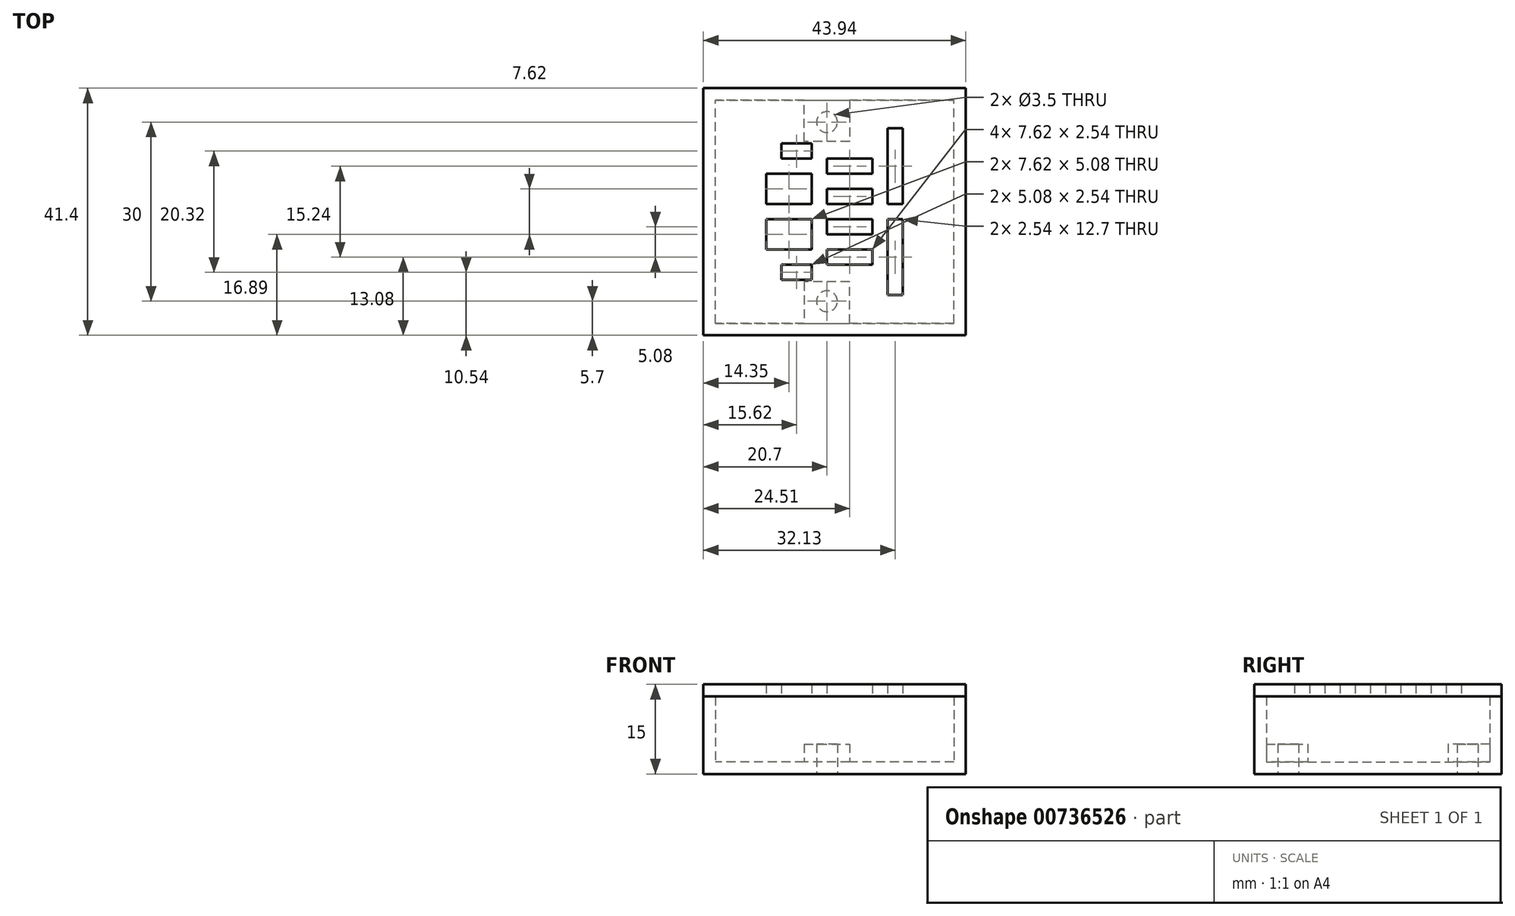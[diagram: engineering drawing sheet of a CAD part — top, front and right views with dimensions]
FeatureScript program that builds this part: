
annotation { "Feature Type Name" : "Feature", "Feature Type Description" : "" }
export const myFeature = defineFeature(function(context is Context, id is Id, definition is map)
    precondition{}
    {
        {
            var Q0;
            Q0=qCreatedBy(makeId("Top.planeOp"),FACE);
            var sketch = newSketch(context, id + "F0", { "sketchPlane" : qUnion([Q0])});
            skLineSegment(sketch, "E0.bottom", {"start": v(-13.97, 12.7) * mm, "end": v(13.97, 12.7) * mm, "construction": true});
            skLineSegment(sketch, "E0.top", {"start": v(-13.97, -12.7) * mm, "end": v(13.97, -12.7) * mm, "construction": true});
            skLineSegment(sketch, "E0.left", {"start": v(-13.97, 12.7) * mm, "end": v(-13.97, -12.7) * mm, "construction": true});
            skLineSegment(sketch, "E0.right", {"start": v(13.97, 12.7) * mm, "end": v(13.97, -12.7) * mm, "construction": true});
            skCircle(sketch, "E1", {"center": v(-13.97, 12.7) * mm, "radius": 1.25 * mm, "construction": true});
            skCircle(sketch, "E2", {"center": v(13.97, 12.7) * mm, "radius": 1.25 * mm, "construction": true});
            skCircle(sketch, "E3", {"center": v(13.97, -12.7) * mm, "radius": 1.25 * mm, "construction": true});
            skCircle(sketch, "E4", {"center": v(-13.97, -12.7) * mm, "radius": 1.25 * mm, "construction": true});
            skLineSegment(sketch, "E5.0", {"start": v(-19.97, 18.7) * mm, "end": v(-19.97, -18.7) * mm});
            skLineSegment(sketch, "E5.1", {"start": v(-19.97, 18.7) * mm, "end": v(19.97, 18.7) * mm});
            skLineSegment(sketch, "E5.2", {"start": v(19.97, 18.7) * mm, "end": v(19.97, -18.7) * mm});
            skLineSegment(sketch, "E5.3", {"start": v(-19.97, -18.7) * mm, "end": v(19.97, -18.7) * mm});
            skLineSegment(sketch, "E6.0", {"start": v(-21.97, 20.7) * mm, "end": v(-21.97, -20.7) * mm});
            skLineSegment(sketch, "E6.1", {"start": v(-21.97, 20.7) * mm, "end": v(21.97, 20.7) * mm});
            skLineSegment(sketch, "E6.2", {"start": v(21.97, 20.7) * mm, "end": v(21.97, -20.7) * mm});
            skLineSegment(sketch, "E6.3", {"start": v(-21.97, -20.7) * mm, "end": v(21.97, -20.7) * mm});
            skLineSegment(sketch, "E7", {"start": v(-1.27, -15) * mm, "end": v(-1.27, 15) * mm, "construction": true});
            skPoint(sketch, "E8", {"position": v(-1.27, 0) * mm});
            skCircle(sketch, "E9", {"center": v(-1.27, 15) * mm, "radius": 1.75 * mm});
            skCircle(sketch, "E10", {"center": v(-1.27, -15) * mm, "radius": 1.75 * mm});
            skLineSegment(sketch, "E11", {"start": v(-5.08, 18.7) * mm, "end": v(-5.08, 11.75) * mm});
            skLineSegment(sketch, "E12", {"start": v(-5.08, 11.75) * mm, "end": v(2.54, 11.75) * mm});
            skLineSegment(sketch, "E13", {"start": v(2.54, 11.75) * mm, "end": v(2.54, 18.7) * mm});
            skPoint(sketch, "E14", {"position": v(-1.27, 11.75) * mm});
            skLineSegment(sketch, "E15", {"start": v(-5.08, -18.7) * mm, "end": v(-5.08, -11.75) * mm});
            skLineSegment(sketch, "E16", {"start": v(-5.08, -11.75) * mm, "end": v(2.54, -11.75) * mm});
            skLineSegment(sketch, "E17", {"start": v(2.54, -11.75) * mm, "end": v(2.54, -18.7) * mm});
            skSolve(sketch);
        }
        {
            var Q0;
            Q0=qSketchRegion(id+"F0",true);
            var Q1;
            Q1=makeQuery(id+"F0.imprint","IMPRINT",FACE,{"disambiguationData":[TD([[makeQuery(id+"F0.imprint","IMPRINT",EDGE,{"derivedFrom":sQuery(id+"F0.wireOp",EDGE,"E5.0")}),1.0]])]});
            var Q2;
            Q2=makeQuery(id+"F0.imprint","IMPRINT",FACE,{"disambiguationData":[TD([[makeQuery(id+"F0.imprint","IMPRINT",EDGE,{"derivedFrom":sQuery(id+"F0.wireOp",EDGE,"E4")}),-1.0]])]});
            var Q3;
            Q3=makeQuery(id+"F0.imprint","IMPRINT",FACE,{"disambiguationData":[TD([[makeQuery(id+"F0.imprint","IMPRINT",EDGE,{"derivedFrom":sQuery(id+"F0.wireOp",EDGE,"E1")}),-1.0]])]});
            var Q4;
            Q4=makeQuery(id+"F0.imprint","IMPRINT",FACE,{"disambiguationData":[TD([[makeQuery(id+"F0.imprint","IMPRINT",EDGE,{"derivedFrom":sQuery(id+"F0.wireOp",EDGE,"E2")}),-1.0]])]});
            var Q5;
            Q5=makeQuery(id+"F0.imprint","IMPRINT",FACE,{"disambiguationData":[TD([[makeQuery(id+"F0.imprint","IMPRINT",EDGE,{"derivedFrom":sQuery(id+"F0.wireOp",EDGE,"E3")}),-1.0]])]});
            var Q6;
            Q6=makeQuery(id+"F0.imprint","IMPRINT",FACE,{"disambiguationData":[TD([[makeQuery(id+"F0.imprint","IMPRINT",EDGE,{"derivedFrom":sQuery(id+"F0.wireOp",EDGE,"E9")}),-1.0]])]});
            var Q7;
            Q7=makeQuery(id+"F0.imprint","IMPRINT",FACE,{"disambiguationData":[TD([[makeQuery(id+"F0.imprint","IMPRINT",EDGE,{"derivedFrom":sQuery(id+"F0.wireOp",EDGE,"E10")}),-1.0]])]});
            extrude(context, id + "F1", {"entities" : qUnion([Q0, Q1, Q2, Q3, Q4, Q5, Q6, Q7]), "depth" : 2 * mm, "offsetDistance" : 25 * mm});
        }
        {
            var Q0;
            Q0=makeQuery(id+"F0.imprint","IMPRINT",FACE,{"disambiguationData":[TD([[makeQuery(id+"F0.imprint","IMPRINT",EDGE,{"derivedFrom":sQuery(id+"F0.wireOp",EDGE,"E5.0")}),-1.0]])]});
            var Q1;
            Q1=makeQuery(id+"F0.imprint","IMPRINT",FACE,{"disambiguationData":[TD([[makeQuery(id+"F0.imprint","IMPRINT",EDGE,{"derivedFrom":sQuery(id+"F0.wireOp",EDGE,"E3")}),-1.0]])]});
            var Q2;
            Q2=makeQuery(id+"F0.imprint","IMPRINT",FACE,{"disambiguationData":[TD([[makeQuery(id+"F0.imprint","IMPRINT",EDGE,{"derivedFrom":sQuery(id+"F0.wireOp",EDGE,"E4")}),-1.0]])]});
            var Q3;
            Q3=makeQuery(id+"F0.imprint","IMPRINT",FACE,{"disambiguationData":[TD([[makeQuery(id+"F0.imprint","IMPRINT",EDGE,{"derivedFrom":sQuery(id+"F0.wireOp",EDGE,"E1")}),-1.0]])]});
            var Q4;
            Q4=makeQuery(id+"F0.imprint","IMPRINT",FACE,{"disambiguationData":[TD([[makeQuery(id+"F0.imprint","IMPRINT",EDGE,{"derivedFrom":sQuery(id+"F0.wireOp",EDGE,"E2")}),-1.0]])]});
            extrude(context, id + "F2", {"entities" : qUnion([Q0, Q1, Q2, Q3, Q4]), "operationType" : NewBodyOperationType.ADD, "depth" : 13 * mm, "offsetDistance" : 25 * mm});
        }
        {
            var Q0;
            Q0=makeQuery(id+"F0.imprint","IMPRINT",FACE,{"disambiguationData":[TD([[makeQuery(id+"F0.imprint","IMPRINT",EDGE,{"derivedFrom":sQuery(id+"F0.wireOp",EDGE,"E9")}),-1.0]])]});
            var Q1;
            Q1=makeQuery(id+"F0.imprint","IMPRINT",FACE,{"disambiguationData":[TD([[makeQuery(id+"F0.imprint","IMPRINT",EDGE,{"derivedFrom":sQuery(id+"F0.wireOp",EDGE,"E10")}),-1.0]])]});
            extrude(context, id + "F3", {"entities" : qUnion([Q0, Q1]), "operationType" : NewBodyOperationType.ADD, "depth" : 5 * mm, "offsetDistance" : 25 * mm});
        }
        {
            var Q0;
            Q0=makeQuery(id+"F2.opExtrude","CAP_FACE",FACE,{"disambiguationData":[OSD([sQuery(id+"F0.wireOp",EDGE,"E5.0"),sQuery(id+"F0.wireOp",EDGE,"E5.1"),sQuery(id+"F0.wireOp",EDGE,"E5.2"),sQuery(id+"F0.wireOp",EDGE,"E5.3"),sQuery(id+"F0.wireOp",EDGE,"E6.0"),sQuery(id+"F0.wireOp",EDGE,"E6.1"),sQuery(id+"F0.wireOp",EDGE,"E6.2"),sQuery(id+"F0.wireOp",EDGE,"E6.3")])],"isStart":false});
            var sketch = newSketch(context, id + "F4", { "sketchPlane" : qUnion([Q0])});
            skLineSegment(sketch, "E18.0", {"start": v(-21.97, 20.7) * mm, "end": v(-21.97, -20.7) * mm});
            skLineSegment(sketch, "E18.1", {"start": v(-21.97, 20.7) * mm, "end": v(21.97, 20.7) * mm});
            skLineSegment(sketch, "E18.2", {"start": v(-21.97, -20.7) * mm, "end": v(21.97, -20.7) * mm});
            skLineSegment(sketch, "E18.3", {"start": v(21.97, 20.7) * mm, "end": v(21.97, -20.7) * mm});
            skLineSegment(sketch, "E19", {"start": v(-21.97, 0) * mm, "end": v(21.97, 0) * mm, "construction": true});
            skLineSegment(sketch, "E20.bottom", {"start": v(8.9, 13.97) * mm, "end": v(11.43, 13.97) * mm});
            skLineSegment(sketch, "E20.top", {"start": v(8.9, 1.27) * mm, "end": v(11.43, 1.27) * mm});
            skLineSegment(sketch, "E20.left", {"start": v(8.9, 13.97) * mm, "end": v(8.9, 11.43) * mm});
            skLineSegment(sketch, "E20.right", {"start": v(11.43, 13.97) * mm, "end": v(11.43, 1.27) * mm});
            skCircle(sketch, "E21.0", {"center": v(-13.97, 12.7) * mm, "radius": 1.25 * mm, "construction": true});
            skCircle(sketch, "E21.1", {"center": v(13.97, 12.7) * mm, "radius": 1.25 * mm, "construction": true});
            skCircle(sketch, "E21.2", {"center": v(13.97, -12.7) * mm, "radius": 1.25 * mm, "construction": true});
            skCircle(sketch, "E21.3", {"center": v(-13.97, -12.7) * mm, "radius": 1.25 * mm, "construction": true});
            skLineSegment(sketch, "E22.bottom", {"start": v(-1.27, 3.8) * mm, "end": v(6.35, 3.8) * mm});
            skLineSegment(sketch, "E22.top", {"start": v(-1.27, 1.27) * mm, "end": v(6.35, 1.27) * mm});
            skLineSegment(sketch, "E22.left", {"start": v(-1.27, 3.8) * mm, "end": v(-1.27, 1.27) * mm});
            skLineSegment(sketch, "E22.right", {"start": v(6.35, 3.8) * mm, "end": v(6.35, 1.27) * mm});
            skLineSegment(sketch, "E23.bottom", {"start": v(-11.43, 6.35) * mm, "end": v(-3.8, 6.35) * mm});
            skLineSegment(sketch, "E23.top", {"start": v(-11.43, 1.27) * mm, "end": v(-3.8, 1.27) * mm});
            skLineSegment(sketch, "E23.left", {"start": v(-11.43, 6.35) * mm, "end": v(-11.43, 1.27) * mm});
            skLineSegment(sketch, "E23.right", {"start": v(-3.8, 6.35) * mm, "end": v(-3.8, 1.27) * mm});
            skLineSegment(sketch, "E24", {"start": v(10.16, 13.97) * mm, "end": v(10.16, 1.27) * mm, "construction": true});
            skLineSegment(sketch, "E25", {"start": v(8.9, 12.7) * mm, "end": v(11.43, 12.7) * mm, "construction": true});
            skLineSegment(sketch, "E26", {"start": v(8.9, 11.43) * mm, "end": v(8.9, 1.27) * mm});
            skPoint(sketch, "E27", {"position": v(10.16, 12.7) * mm});
            skLineSegment(sketch, "E28.bottom", {"start": v(-1.27, 8.9) * mm, "end": v(6.35, 8.9) * mm});
            skLineSegment(sketch, "E28.top", {"start": v(-1.27, 6.35) * mm, "end": v(6.35, 6.35) * mm});
            skLineSegment(sketch, "E28.left", {"start": v(-1.27, 8.9) * mm, "end": v(-1.27, 6.35) * mm});
            skLineSegment(sketch, "E28.right", {"start": v(6.35, 8.9) * mm, "end": v(6.35, 6.35) * mm});
            skLineSegment(sketch, "E29.bottom", {"start": v(-8.89, 11.43) * mm, "end": v(-3.8, 11.43) * mm});
            skLineSegment(sketch, "E29.top", {"start": v(-8.89, 8.9) * mm, "end": v(-3.8, 8.9) * mm});
            skLineSegment(sketch, "E29.left", {"start": v(-8.89, 11.43) * mm, "end": v(-8.89, 8.9) * mm});
            skLineSegment(sketch, "E29.right", {"start": v(-3.8, 11.43) * mm, "end": v(-3.8, 8.9) * mm});
            skLineSegment(sketch, "E30.MirrorCS", {"start": v(-11.43, -1.27) * mm, "end": v(-3.8, -1.27) * mm});
            skLineSegment(sketch, "E31.MirrorCS", {"start": v(-3.8, -6.35) * mm, "end": v(-3.8, -1.27) * mm});
            skLineSegment(sketch, "E32.MirrorCS", {"start": v(-11.43, -6.35) * mm, "end": v(-3.8, -6.35) * mm});
            skLineSegment(sketch, "E33.MirrorCS", {"start": v(-11.43, -6.35) * mm, "end": v(-11.43, -1.27) * mm});
            skLineSegment(sketch, "E34.MirrorCS", {"start": v(-8.89, -8.9) * mm, "end": v(-3.8, -8.9) * mm});
            skLineSegment(sketch, "E35.MirrorCS", {"start": v(-3.8, -11.43) * mm, "end": v(-3.8, -8.9) * mm});
            skLineSegment(sketch, "E36.MirrorCS", {"start": v(-8.89, -11.43) * mm, "end": v(-3.8, -11.43) * mm});
            skLineSegment(sketch, "E37.MirrorCS", {"start": v(-8.89, -11.43) * mm, "end": v(-8.89, -8.9) * mm});
            skLineSegment(sketch, "E38.MirrorCS", {"start": v(-1.27, -8.9) * mm, "end": v(-1.27, -6.35) * mm});
            skLineSegment(sketch, "E39.MirrorCS", {"start": v(-1.27, -8.9) * mm, "end": v(6.35, -8.9) * mm});
            skLineSegment(sketch, "E40.MirrorCS", {"start": v(6.35, -8.9) * mm, "end": v(6.35, -6.35) * mm});
            skLineSegment(sketch, "E41.MirrorCS", {"start": v(-1.27, -6.35) * mm, "end": v(6.35, -6.35) * mm});
            skLineSegment(sketch, "E42.MirrorCS", {"start": v(-1.27, -3.8) * mm, "end": v(6.35, -3.8) * mm});
            skLineSegment(sketch, "E43.MirrorCS", {"start": v(-1.27, -3.8) * mm, "end": v(-1.27, -1.27) * mm});
            skLineSegment(sketch, "E44.MirrorCS", {"start": v(-1.27, -1.27) * mm, "end": v(6.35, -1.27) * mm});
            skLineSegment(sketch, "E45.MirrorCS", {"start": v(6.35, -3.8) * mm, "end": v(6.35, -1.27) * mm});
            skLineSegment(sketch, "E46.MirrorCS", {"start": v(11.43, -13.97) * mm, "end": v(11.43, -1.27) * mm});
            skLineSegment(sketch, "E47.MirrorCS", {"start": v(8.9, -1.27) * mm, "end": v(11.43, -1.27) * mm});
            skLineSegment(sketch, "E48.MirrorCS", {"start": v(8.9, -13.97) * mm, "end": v(11.43, -13.97) * mm});
            skLineSegment(sketch, "E49", {"start": v(8.9, -1.27) * mm, "end": v(8.9, -13.97) * mm});
            skSolve(sketch);
        }
        {
            var Q0;
            Q0=qSketchRegion(id+"F4",true);
            extrude(context, id + "F5", {"entities" : qUnion([Q0]), "depth" : 2 * mm, "offsetDistance" : 25 * mm});
        }
    });
